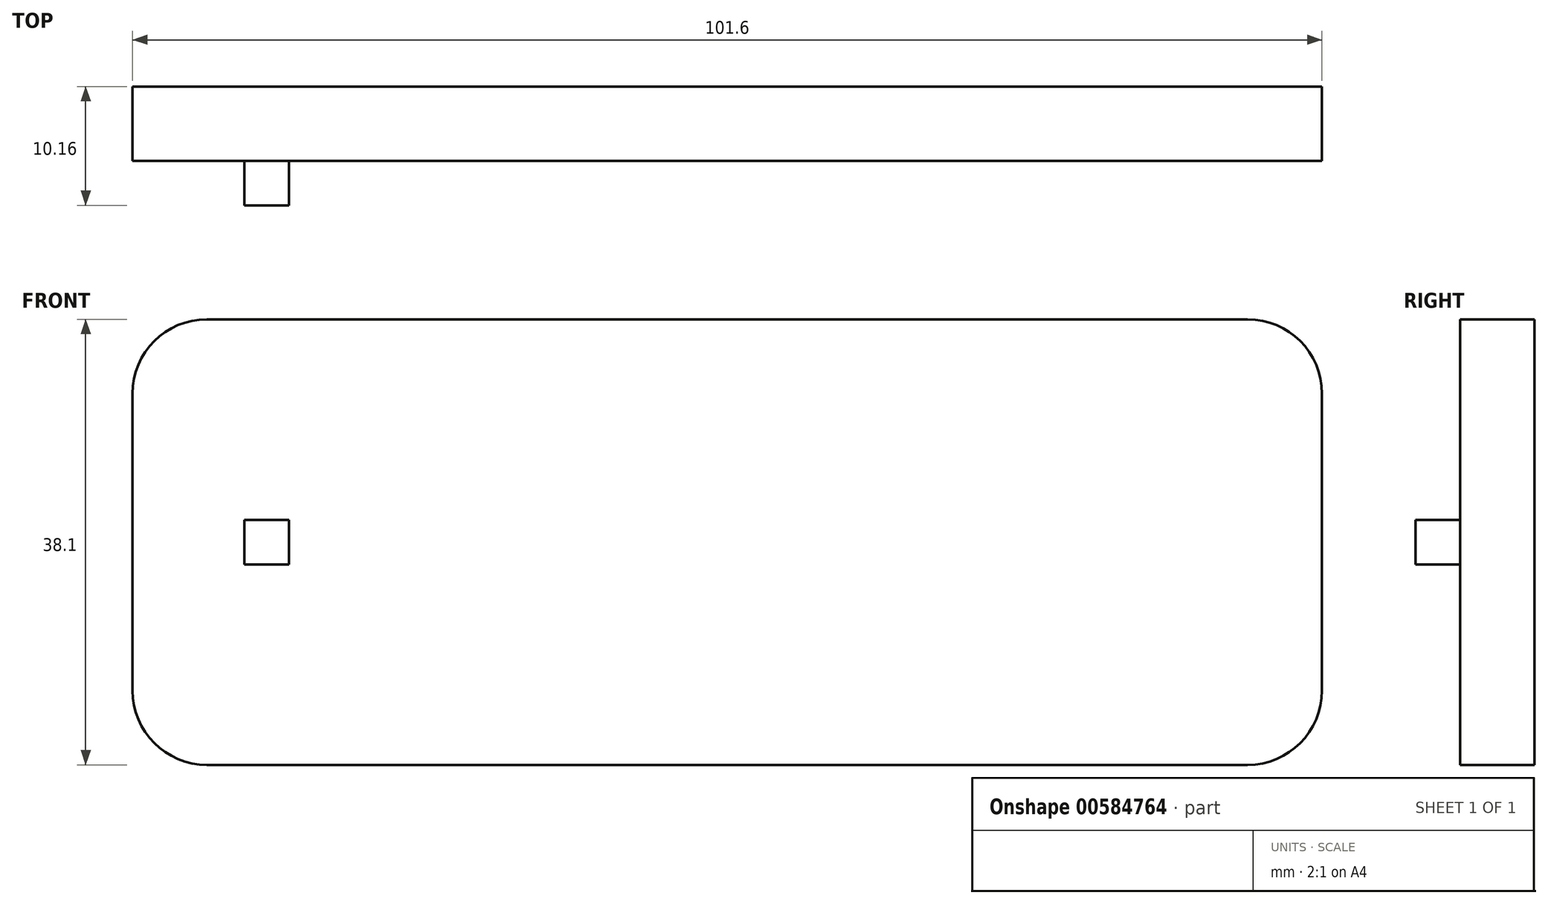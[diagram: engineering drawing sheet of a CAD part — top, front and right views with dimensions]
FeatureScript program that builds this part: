
annotation { "Feature Type Name" : "Feature", "Feature Type Description" : "" }
export const myFeature = defineFeature(function(context is Context, id is Id, definition is map)
    precondition{}
    {
        {
            var Q0;
            Q0=qCreatedBy(makeId("Front.planeOp"),FACE);
            var sketch = newSketch(context, id + "F0", { "sketchPlane" : qUnion([Q0])});
            skLineSegment(sketch, "E0.bottom", {"start": v(-44.45, -19.05) * mm, "end": v(44.45, -19.05) * mm});
            skLineSegment(sketch, "E0.top", {"start": v(-44.45, 19.05) * mm, "end": v(44.45, 19.05) * mm});
            skLineSegment(sketch, "E0.left", {"start": v(-50.8, -12.7) * mm, "end": v(-50.8, 12.7) * mm});
            skLineSegment(sketch, "E0.right", {"start": v(50.8, -12.7) * mm, "end": v(50.8, 12.7) * mm});
            skPoint(sketch, "E0.middle", {"position": v(0, 0) * mm});
            skPoint(sketch, "E1.visualSharp", {"position": v(-50.8, 19.05) * mm});
            skArc(sketch, "E1.filletArc", {"start": v(-44.45, 19.05) * mm, "mid": v(-48.94, 17.2) * mm, "end": v(-50.8, 12.7) * mm});
            skPoint(sketch, "E2.visualSharp", {"position": v(-50.8, -19.05) * mm});
            skArc(sketch, "E2.filletArc", {"start": v(-50.8, -12.7) * mm, "mid": v(-48.94, -17.2) * mm, "end": v(-44.45, -19.05) * mm});
            skPoint(sketch, "E3.visualSharp", {"position": v(50.8, 19.05) * mm});
            skArc(sketch, "E3.filletArc", {"start": v(50.8, 12.7) * mm, "mid": v(48.94, 17.2) * mm, "end": v(44.45, 19.05) * mm});
            skPoint(sketch, "E4.visualSharp", {"position": v(50.8, -19.05) * mm});
            skArc(sketch, "E4.filletArc", {"start": v(44.45, -19.05) * mm, "mid": v(48.94, -17.2) * mm, "end": v(50.8, -12.7) * mm});
            skSolve(sketch);
        }
        {
            var Q0;
            Q0=makeQuery(id+"F0.imprint","IMPRINT",FACE,{"disambiguationData":[TD([[makeQuery(id+"F0.imprint","IMPRINT",EDGE,{"derivedFrom":sQuery(id+"F0.wireOp",EDGE,"E0.bottom")}),1.0]])]});
            extrude(context, id + "F1", {"entities" : qUnion([Q0]), "depth" : 6.35 * mm, "offsetDistance" : 25.4 * mm});
        }
        {
            var Q0;
            Q0=makeQuery(id+"F1.opExtrude","CAP_FACE",FACE,{"disambiguationData":[OSD([sQuery(id+"F0.wireOp",EDGE,"E0.bottom"),sQuery(id+"F0.wireOp",EDGE,"E0.top"),sQuery(id+"F0.wireOp",EDGE,"E0.left"),sQuery(id+"F0.wireOp",EDGE,"E0.right"),sQuery(id+"F0.wireOp",EDGE,"E1.filletArc"),sQuery(id+"F0.wireOp",EDGE,"E2.filletArc"),sQuery(id+"F0.wireOp",EDGE,"E3.filletArc"),sQuery(id+"F0.wireOp",EDGE,"E4.filletArc")])],"isStart":false});
            var sketch = newSketch(context, id + "F2", { "sketchPlane" : qUnion([Q0])});
            skLineSegment(sketch, "E5.bottom", {"start": v(-37.43, -1.9) * mm, "end": v(-41.24, -1.9) * mm});
            skLineSegment(sketch, "E5.top", {"start": v(-37.43, 1.9) * mm, "end": v(-41.24, 1.9) * mm});
            skLineSegment(sketch, "E5.left", {"start": v(-37.43, -1.9) * mm, "end": v(-37.43, 1.9) * mm});
            skLineSegment(sketch, "E5.right", {"start": v(-41.24, -1.9) * mm, "end": v(-41.24, 1.9) * mm});
            skPoint(sketch, "E5.middle", {"position": v(-39.33, 0) * mm});
            skSolve(sketch);
        }
        {
            var Q0;
            Q0=makeQuery(id+"F2.imprint","IMPRINT",FACE,{"disambiguationData":[TD([[makeQuery(id+"F2.imprint","IMPRINT",EDGE,{"derivedFrom":sQuery(id+"F2.wireOp",EDGE,"E5.bottom")}),-1.0]])]});
            extrude(context, id + "F3", {"entities" : qUnion([Q0]), "operationType" : NewBodyOperationType.ADD, "depth" : 3.8 * mm, "offsetDistance" : 25.4 * mm});
        }
    });
